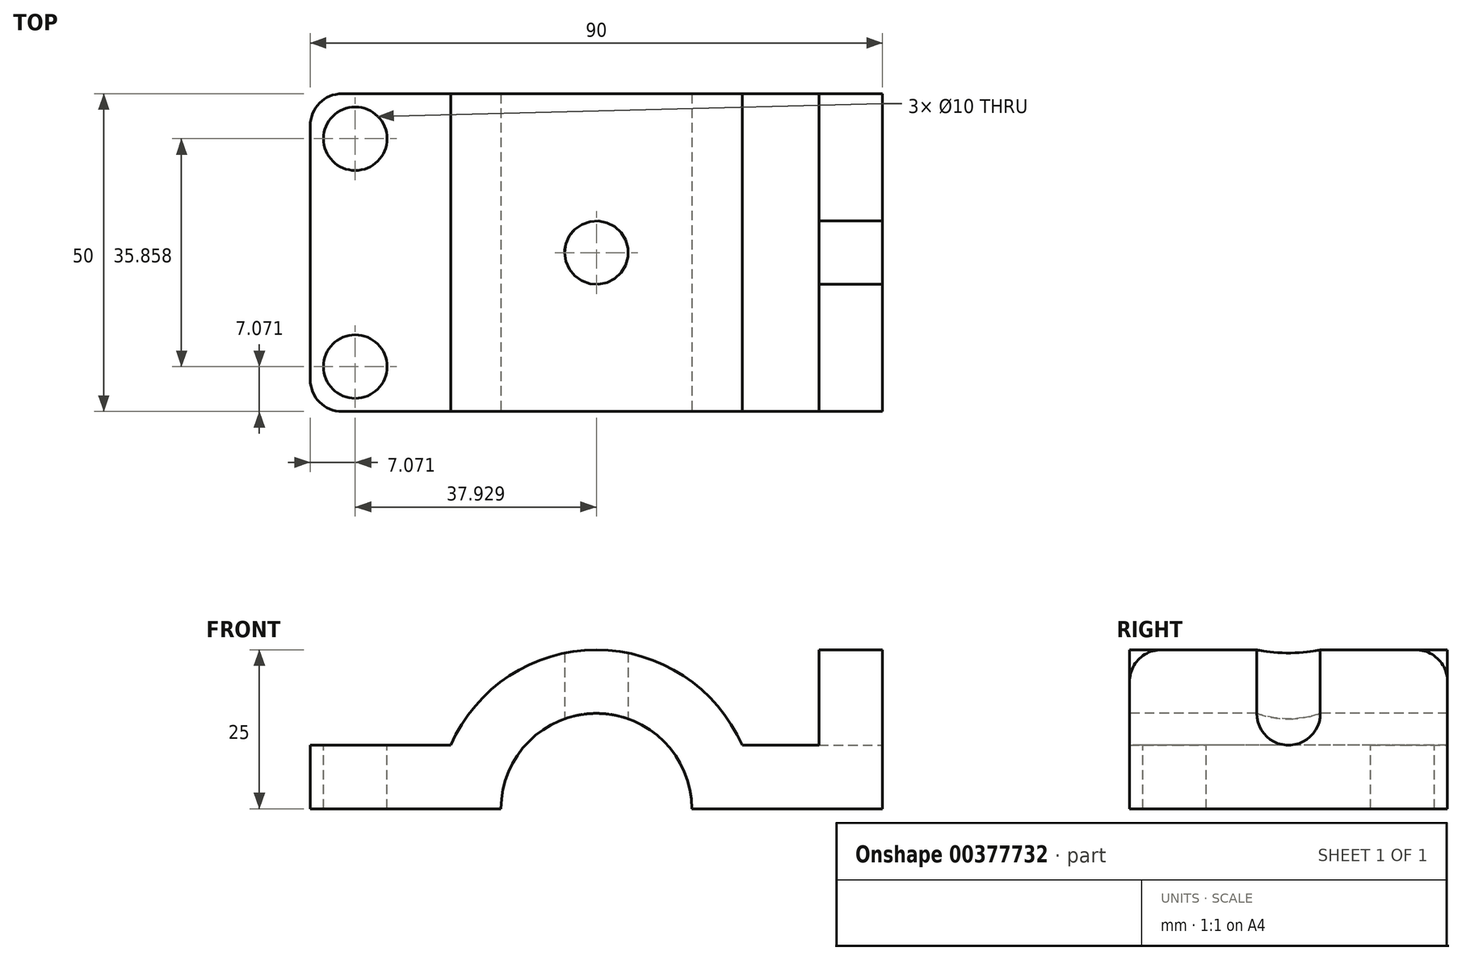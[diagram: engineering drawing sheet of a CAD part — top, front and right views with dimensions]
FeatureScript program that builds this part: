
annotation { "Feature Type Name" : "Feature", "Feature Type Description" : "" }
export const myFeature = defineFeature(function(context is Context, id is Id, definition is map)
    precondition{}
    {
        {
            var Q0;
            Q0=qCreatedBy(makeId("Front.planeOp"),FACE);
            var sketch = newSketch(context, id + "F0", { "sketchPlane" : qUnion([Q0])});
            skLineSegment(sketch, "E0", {"start": v(0, 0) * mm, "end": v(30, 0) * mm});
            skLineSegment(sketch, "E1", {"start": v(60, 0) * mm, "end": v(90, 0) * mm});
            skLineSegment(sketch, "E2", {"start": v(90, 0) * mm, "end": v(90, 25) * mm});
            skArc(sketch, "E3", {"start": v(60, 0) * mm, "mid": v(45, 15) * mm, "end": v(30, 0) * mm});
            skLineSegment(sketch, "E4.0", {"start": v(80, 10) * mm, "end": v(80, 25) * mm});
            skLineSegment(sketch, "E4.1", {"start": v(67.91, 10) * mm, "end": v(80, 10) * mm});
            skArc(sketch, "E4.2", {"start": v(67.91, 10) * mm, "mid": v(45, 25) * mm, "end": v(22.09, 10) * mm});
            skLineSegment(sketch, "E4.3", {"start": v(0, 10) * mm, "end": v(22.09, 10) * mm});
            skLineSegment(sketch, "E5", {"start": v(80, 25) * mm, "end": v(90, 25) * mm});
            skLineSegment(sketch, "E6", {"start": v(0, 10) * mm, "end": v(0, 0) * mm});
            skSolve(sketch);
        }
        {
            var Q0;
            Q0 = qSketchRegion(id + "F0", true);
            extrude(context, id + "F1", {"entities" : qUnion([Q0]), "oppositeDirection" : true, "depth" : 50 * mm});
        }
        {
            var Q0;
            Q0=makeQuery(id+"F1.opExtrude","SWEPT_FACE",FACE,{"disambiguationData":[OSD([sQuery(id+"F0.wireOp",EDGE,"E2")])]});
            var sketch = newSketch(context, id + "F2", { "sketchPlane" : qUnion([Q0])});
            skLineSegment(sketch, "E7", {"start": v(20, 25) * mm, "end": v(20, 15) * mm});
            skLineSegment(sketch, "E8", {"start": v(30, 15) * mm, "end": v(30, 25) * mm});
            skLineSegment(sketch, "E9", {"start": v(30, 25) * mm, "end": v(50, 25) * mm});
            skLineSegment(sketch, "E10", {"start": v(20, 25) * mm, "end": v(0, 25) * mm});
            skArc(sketch, "E11", {"start": v(20, 15) * mm, "mid": v(25, 10) * mm, "end": v(30, 15) * mm});
            skSolve(sketch);
        }
        {
            var Q0;
            {var subQ0=sQuery(id+"F2.wireOp",EDGE,"E7");Q0=makeQuery(id+"F2.imprint","IMPRINT",FACE,{"disambiguationData":[TD([[makeQuery(id+"F2.imprint","IMPRINT",EDGE,{"derivedFrom":subQ0}),1.0]])]});}
            var Q1;
            Q1=makeQuery(id+"F1.opExtrude","SWEPT_FACE",FACE,{"disambiguationData":[OSD([sQuery(id+"F0.wireOp",EDGE,"E4.0")])]});
            extrude(context, id + "F3", {"entities" : qUnion([Q0]), "operationType" : NewBodyOperationType.REMOVE, "endBound" : BoundingType.UP_TO_SURFACE, "oppositeDirection" : true, "endBoundEntityFace" : qUnion([Q1]), "depth" : 25 * mm});
        }
        {
            var Q0;
            Q0=makeQuery(id+"F1.opExtrude","SWEPT_FACE",FACE,{"disambiguationData":[OSD([sQuery(id+"F0.wireOp",EDGE,"E4.3")])]});
            var sketch = newSketch(context, id + "F4", { "sketchPlane" : qUnion([Q0])});
            skLineSegment(sketch, "E12", {"start": v(0, 50) * mm, "end": v(7.07, 42.93) * mm});
            skLineSegment(sketch, "E13", {"start": v(0, 0) * mm, "end": v(7.07, 7.07) * mm});
            skCircle(sketch, "E14", {"center": v(7.07, 42.93) * mm, "radius": 5 * mm});
            skCircle(sketch, "E15", {"center": v(7.07, 7.07) * mm, "radius": 5 * mm});
            skSolve(sketch);
        }
        {
            var Q0;
            Q0=makeQuery(id+"F4.imprint","IMPRINT",FACE,{"disambiguationData":[TD([[makeQuery(id+"F4.imprint","IMPRINT",EDGE,{"derivedFrom":sQuery(id+"F4.wireOp",EDGE,"E14")}),1.0]])]});
            var Q1;
            Q1=makeQuery(id+"F4.imprint","IMPRINT",FACE,{"disambiguationData":[TD([[makeQuery(id+"F4.imprint","IMPRINT",EDGE,{"derivedFrom":sQuery(id+"F4.wireOp",EDGE,"E15")}),1.0]])]});
            var Q2;
            Q2=makeQuery(id+"F1.opExtrude","SWEPT_FACE",FACE,{"disambiguationData":[OSD([sQuery(id+"F0.wireOp",EDGE,"E0")])]});
            extrude(context, id + "F5", {"entities" : qUnion([Q0, Q1]), "operationType" : NewBodyOperationType.REMOVE, "endBound" : BoundingType.UP_TO_SURFACE, "oppositeDirection" : true, "endBoundEntityFace" : qUnion([Q2]), "depth" : 25 * mm});
        }
        {
            var Q0;
            Q0=qCreatedBy(makeId("Top.planeOp"),FACE);
            var sketch = newSketch(context, id + "F6", { "sketchPlane" : qUnion([Q0])});
            skLineSegment(sketch, "E16", {"start": v(0, 0) * mm, "end": v(45, 0) * mm});
            skLineSegment(sketch, "E17", {"start": v(45, 0) * mm, "end": v(45, 25) * mm});
            skCircle(sketch, "E18", {"center": v(45, 25) * mm, "radius": 5 * mm});
            skSolve(sketch);
        }
        {
            var Q0;
            Q0=makeQuery(id+"F6.imprint","IMPRINT",FACE,{"disambiguationData":[TD([[makeQuery(id+"F6.imprint","IMPRINT",EDGE,{"derivedFrom":sQuery(id+"F6.wireOp",EDGE,"E18")}),1.0]])]});
            var Q1;
            Q1=sQuery(id+"F6.wireOp",EDGE,"E18");
            var Q2;
            Q2=makeQuery(id+"F1.opExtrude","SWEPT_FACE",FACE,{"disambiguationData":[OSD([sQuery(id+"F0.wireOp",EDGE,"E4.2")])]});
            extrude(context, id + "F7", {"entities" : qUnion([Q0]), "operationType" : NewBodyOperationType.REMOVE, "surfaceEntities" : qUnion([Q1]), "endBound" : BoundingType.UP_TO_SURFACE, "endBoundEntityFace" : qUnion([Q2]), "depth" : 40 * mm});
        }
        {
            var Q0;
            Q0=makeQuery(id+"F1.opExtrude","CAP_EDGE",EDGE,{"disambiguationData":[OSD([sQuery(id+"F0.wireOp",EDGE,"E6")])],"isStart":true});
            var Q1;
            Q1=makeQuery(id+"F1.opExtrude","CAP_EDGE",EDGE,{"disambiguationData":[OSD([sQuery(id+"F0.wireOp",EDGE,"E6")])],"isStart":false});
            fillet(context, id + "F8", {"entities" : qUnion([Q0, Q1]), "radius" : 5 * mm, "tangentPropagation" : true, "allowEdgeOverflow" : false});
        }
        {
            var Q0;
            Q0=makeQuery(id+"F1.opExtrude","CAP_EDGE",EDGE,{"disambiguationData":[OSD([sQuery(id+"F0.wireOp",EDGE,"E5")])],"isStart":true});
            var Q1;
            Q1=makeQuery(id+"F1.opExtrude","CAP_EDGE",EDGE,{"disambiguationData":[OSD([sQuery(id+"F0.wireOp",EDGE,"E5")])],"isStart":false});
            fillet(context, id + "F9", {"entities" : qUnion([Q0, Q1]), "radius" : 5 * mm, "tangentPropagation" : true, "allowEdgeOverflow" : false});
        }
    });
